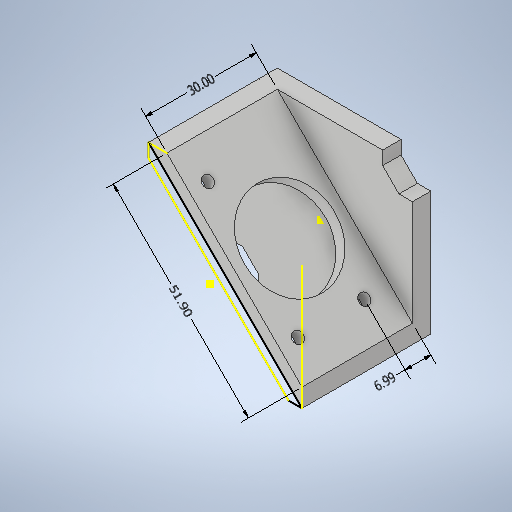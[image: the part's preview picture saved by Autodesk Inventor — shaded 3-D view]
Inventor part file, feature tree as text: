
AUTODESK INVENTOR PART (.ipt)
format: ipt  version: 2025 (Build 290162000, 162)  size: 331,776 bytes
history: native  units: mm
features: sketch x8, hole x4, extrude x3, other x3
ambient origin geometry x8: Origin, YZ Plane, XZ Plane, XY Plane, X Axis, Y Axis, Z Axis, Center Point
bodies: 实体1 (feature_tree)
feature tree (18):
  extrude  "拉伸1"  Depth=30.0mm TaperAngle=0.0deg
  sketch  "草图2"  dims[d12=24.5mm d13=6.0mm d14=4.0mm d15=2.0mm d16=90.0deg d17=8.0mm d18=20.594885mm]
  extrude  "拉伸2"  Depth=30.0mm TaperAngle=0.0deg
  hole  "孔1"  [1 undecoded]
  hole  "孔2"  [1 undecoded]
  extrude  "拉伸3"  Depth=30.0mm
  hole  "孔3"  [1 undecoded]
  hole  "孔4"  [1 undecoded]
  sketch  "草图1"  dims[d8=5.0mm d9=0.0mm d10=30.0mm d11=0.0mm]
  sketch  "草图3"  dims[d19=0.01mm d20=6.0mm d21=4.0mm d22=2.0mm d23=90.0deg d24=8.0mm d25=20.594885mm d26=30.0mm d27=0.0mm]
  sketch  "草图4"  dims[d36=2.97mm d37=6.0mm d38=4.0mm d39=2.0mm d40=90.0deg d41=0.5mm d42=20.594885mm]
  sketch  "草图5"  dims[d43=2.0mm]
  sketch  "草图6"  dims[d44=2.97mm d45=6.0mm d46=4.0mm d47=2.0mm d48=90.0deg d49=0.5mm d50=20.594885mm]
  sketch  "草图7"  dims[d28=6.575673mm d29=8.362671mm d30=51.90253mm d31=8.575597mm d32=30.0mm d51=75.905008mm d52=8.236956mm d53=6.991479mm d33=1.0mm]
  sketch  "草图8"  dims[d34=1.0mm d35=1.0mm]
  other  "线性尺寸 1"
  other  "线性尺寸 2"
  other  "线性尺寸 3"
note: 4 required parameter values undecoded (feature->parameter linkage not recoverable at this tier; creation-order binding heuristic only, values carry confidence <= 0.55)
